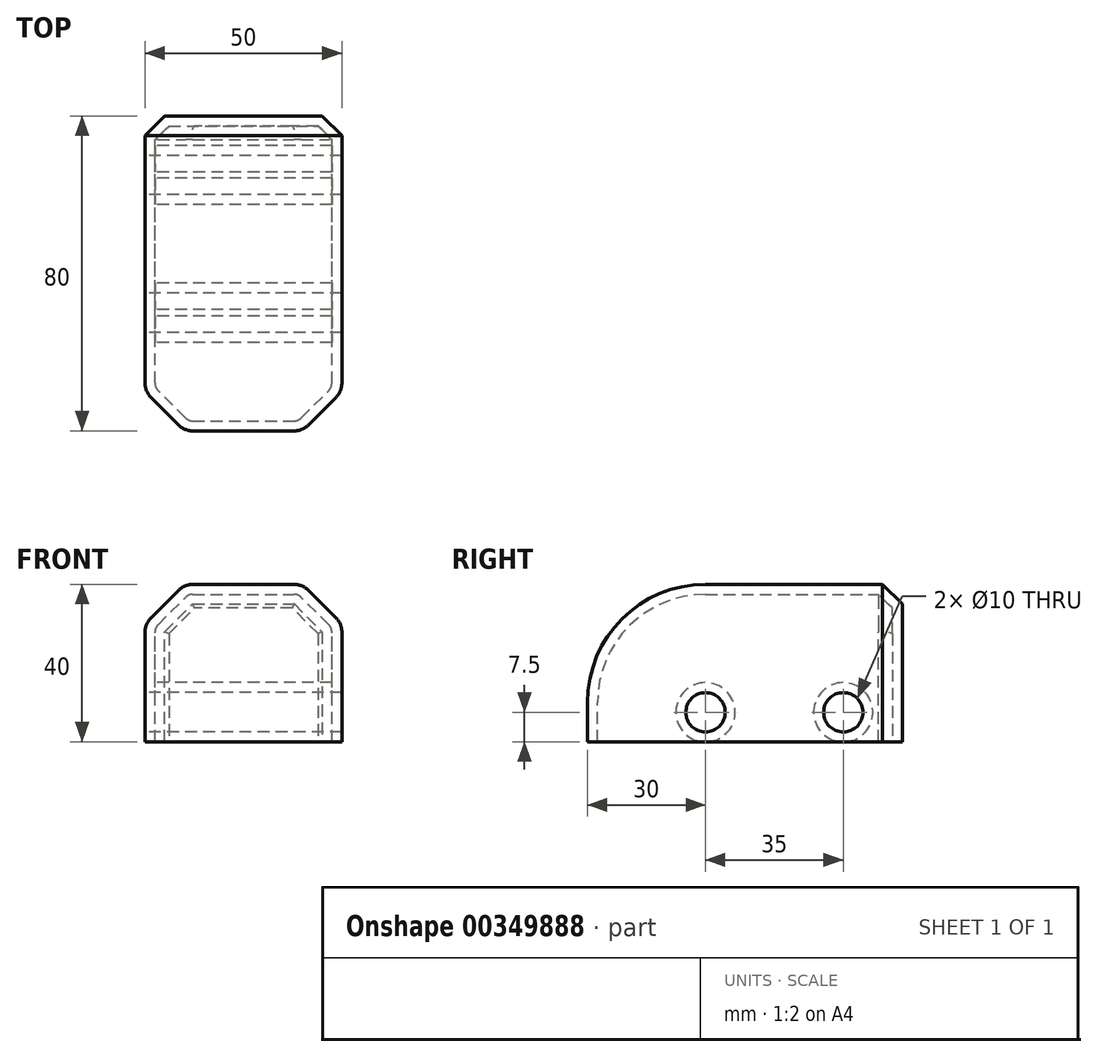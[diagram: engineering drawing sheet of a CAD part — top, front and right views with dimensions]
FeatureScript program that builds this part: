
annotation { "Feature Type Name" : "Feature", "Feature Type Description" : "" }
export const myFeature = defineFeature(function(context is Context, id is Id, definition is map)
    precondition{}
    {
        {
            var Q0;
            Q0=qCreatedBy(makeId("Top.planeOp"),FACE);
            var sketch = newSketch(context, id + "F0", { "sketchPlane" : qUnion([Q0])});
            skLineSegment(sketch, "E0.bottom", {"start": v(0, 0) * mm, "end": v(50, 0) * mm});
            skLineSegment(sketch, "E0.top", {"start": v(0, 80) * mm, "end": v(50, 80) * mm});
            skLineSegment(sketch, "E0.left", {"start": v(0, 0) * mm, "end": v(0, 80) * mm});
            skLineSegment(sketch, "E0.right", {"start": v(50, 0) * mm, "end": v(50, 80) * mm});
            skSolve(sketch);
        }
        {
            var Q0;
            Q0=qSketchRegion(id+"F0",true);
            var Q1;
            Q1=makeQuery(id+"F0.imprint","IMPRINT",FACE,{"disambiguationData":[TD([[makeQuery(id+"F0.imprint","IMPRINT",EDGE,{"derivedFrom":sQuery(id+"F0.wireOp",EDGE,"E0.bottom")}),1.0]])]});
            extrude(context, id + "F1", {"entities" : qUnion([Q0, Q1]), "depth" : 40 * mm});
        }
        {
            var Q0;
            Q0=makeQuery(id+"F1.opExtrude","CAP_EDGE",EDGE,{"disambiguationData":[OSD([sQuery(id+"F0.wireOp",EDGE,"E0.bottom")])],"isStart":false});
            fillet(context, id + "F2", {"entities" : qUnion([Q0]), "radius" : 30 * mm, "tangentPropagation" : true, "allowEdgeOverflow" : false});
        }
        {
            var Q0;
            Q0=makeQuery(id+"F1.opExtrude","CAP_EDGE",EDGE,{"disambiguationData":[OSD([sQuery(id+"F0.wireOp",EDGE,"E0.right")])],"isStart":false});
            var Q1;
            Q1=makeQuery(id+"F1.opExtrude","CAP_EDGE",EDGE,{"disambiguationData":[OSD([sQuery(id+"F0.wireOp",EDGE,"E0.left")])],"isStart":false});
            chamfer(context, id + "F3", {"entities" : qUnion([Q0, Q1]), "width" : 10 * mm, "tangentPropagation" : true});
        }
        {
            var Q0;
            {var subQ0=sQuery(id+"F0.wireOp",EDGE,"E0.right");Q0=makeQuery(id+"F3.opChamfer","BLEND_EDGE",EDGE,{"blendedFrom":[makeQuery(id+"F1.opExtrude","CAP_EDGE",EDGE,{"disambiguationData":[OSD([subQ0])],"isStart":false}),makeQuery(id+"F1.opExtrude","CAP_FACE",FACE,{"disambiguationData":[OSD([sQuery(id+"F0.wireOp",EDGE,"E0.bottom"),sQuery(id+"F0.wireOp",EDGE,"E0.top"),sQuery(id+"F0.wireOp",EDGE,"E0.left"),subQ0])],"isStart":false})],"blendedInto":[makeQuery(id+"F1.opExtrude","CAP_FACE",FACE,{"disambiguationData":[OSD([sQuery(id+"F0.wireOp",EDGE,"E0.bottom"),sQuery(id+"F0.wireOp",EDGE,"E0.top"),sQuery(id+"F0.wireOp",EDGE,"E0.left"),subQ0])],"isStart":false})]});}
            var Q1;
            {var subQ0=sQuery(id+"F0.wireOp",EDGE,"E0.left");Q1=makeQuery(id+"F3.opChamfer","BLEND_EDGE",EDGE,{"blendedFrom":[makeQuery(id+"F1.opExtrude","CAP_EDGE",EDGE,{"disambiguationData":[OSD([subQ0])],"isStart":false}),makeQuery(id+"F1.opExtrude","CAP_FACE",FACE,{"disambiguationData":[OSD([sQuery(id+"F0.wireOp",EDGE,"E0.bottom"),sQuery(id+"F0.wireOp",EDGE,"E0.top"),subQ0,sQuery(id+"F0.wireOp",EDGE,"E0.right")])],"isStart":false})],"blendedInto":[makeQuery(id+"F1.opExtrude","CAP_FACE",FACE,{"disambiguationData":[OSD([sQuery(id+"F0.wireOp",EDGE,"E0.bottom"),sQuery(id+"F0.wireOp",EDGE,"E0.top"),subQ0,sQuery(id+"F0.wireOp",EDGE,"E0.right")])],"isStart":false})]});}
            fillet(context, id + "F4", {"entities" : qUnion([Q0, Q1]), "radius" : 5.08 * mm, "tangentPropagation" : true, "allowEdgeOverflow" : false});
        }
        {
            var Q0;
            {var subQ0=sQuery(id+"F0.wireOp",EDGE,"E0.right");Q0=makeQuery(id+"F3.opChamfer","BLEND_EDGE",EDGE,{"blendedFrom":[makeQuery(id+"F1.opExtrude","CAP_EDGE",EDGE,{"disambiguationData":[OSD([subQ0])],"isStart":false}),makeQuery(id+"F1.opExtrude","SWEPT_FACE",FACE,{"disambiguationData":[OSD([subQ0])]})],"blendedInto":[makeQuery(id+"F1.opExtrude","SWEPT_FACE",FACE,{"disambiguationData":[OSD([subQ0])]})]});}
            var Q1;
            {var subQ0=sQuery(id+"F0.wireOp",EDGE,"E0.left");Q1=makeQuery(id+"F3.opChamfer","BLEND_EDGE",EDGE,{"blendedFrom":[makeQuery(id+"F1.opExtrude","CAP_EDGE",EDGE,{"disambiguationData":[OSD([subQ0])],"isStart":false}),makeQuery(id+"F1.opExtrude","SWEPT_FACE",FACE,{"disambiguationData":[OSD([subQ0])]})],"blendedInto":[makeQuery(id+"F1.opExtrude","SWEPT_FACE",FACE,{"disambiguationData":[OSD([subQ0])]})]});}
            fillet(context, id + "F5", {"entities" : qUnion([Q0, Q1]), "radius" : 5.08 * mm, "tangentPropagation" : true, "allowEdgeOverflow" : false});
        }
        {
            var Q0;
            Q0=makeQuery(id+"F1.opExtrude","SWEPT_EDGE",EDGE,{"disambiguationData":[OSD([sQuery(id+"F0.wireOp",EDGE,"E0.top"),sQuery(id+"F0.wireOp",EDGE,"E0.right")])]});
            chamfer(context, id + "F6", {"entities" : qUnion([Q0]), "width" : 5 * mm, "tangentPropagation" : true});
        }
        {
            var Q0;
            Q0=makeQuery(id+"F1.opExtrude","SWEPT_FACE",FACE,{"disambiguationData":[OSD([sQuery(id+"F0.wireOp",EDGE,"E0.left")])]});
            var sketch = newSketch(context, id + "F7", { "sketchPlane" : qUnion([Q0])});
            skLineSegment(sketch, "E1.0.0", {"start": v(-30, 27.9) * mm, "end": v(-75, 27.9) * mm});
            skLineSegment(sketch, "E1.0.1", {"start": v(-75, 27.9) * mm, "end": v(-75, 0) * mm});
            skLineSegment(sketch, "E1.0.2", {"start": v(-75, 0) * mm, "end": v(-15.16, 0) * mm});
            skArc(sketch, "E1.0.3", {"start": v(-15.16, 0) * mm, "mid": v(-14.2, 18.4) * mm, "end": v(-30, 27.9) * mm});
            skLineSegment(sketch, "E2", {"start": v(-65, 0) * mm, "end": v(-65, 27.9) * mm, "construction": true});
            skPoint(sketch, "E3", {"position": v(-65, 7.5) * mm});
            skPoint(sketch, "E4", {"position": v(-30, 7.5) * mm});
            skCircle(sketch, "E5", {"center": v(-65, 7.5) * mm, "radius": 5 * mm});
            skLineSegment(sketch, "E6", {"start": v(-30, 27.9) * mm, "end": v(-30, 0) * mm, "construction": true});
            skCircle(sketch, "E7", {"center": v(-30, 7.5) * mm, "radius": 5 * mm});
            skSolve(sketch);
        }
        {
            var Q0;
            Q0=makeQuery(id+"F7.imprint","IMPRINT",FACE,{"disambiguationData":[TD([[makeQuery(id+"F7.imprint","IMPRINT",EDGE,{"derivedFrom":sQuery(id+"F7.wireOp",EDGE,"E5")}),1.0]])]});
            var Q1;
            Q1=makeQuery(id+"F7.imprint","IMPRINT",FACE,{"disambiguationData":[TD([[makeQuery(id+"F7.imprint","IMPRINT",EDGE,{"derivedFrom":sQuery(id+"F7.wireOp",EDGE,"E7")}),1.0]])]});
            var Q2;
            Q2=makeQuery(id+"F1.opExtrude","SWEPT_FACE",FACE,{"disambiguationData":[OSD([sQuery(id+"F0.wireOp",EDGE,"E0.right")])]});
            extrude(context, id + "F8", {"entities" : qUnion([Q0, Q1]), "operationType" : NewBodyOperationType.REMOVE, "endBound" : BoundingType.UP_TO_SURFACE, "oppositeDirection" : true, "endBoundEntityFace" : qUnion([Q2]), "depth" : 25.4 * mm});
        }
        {
            var Q0;
            Q0=makeQuery(id+"F1.opExtrude","CAP_FACE",FACE,{"disambiguationData":[OSD([sQuery(id+"F0.wireOp",EDGE,"E0.bottom"),sQuery(id+"F0.wireOp",EDGE,"E0.top"),sQuery(id+"F0.wireOp",EDGE,"E0.left"),sQuery(id+"F0.wireOp",EDGE,"E0.right")])],"isStart":true});
            shell(context, id + "F9", {"entities" : qUnion([Q0]), "thickness" : 2.54 * mm});
        }
    });
